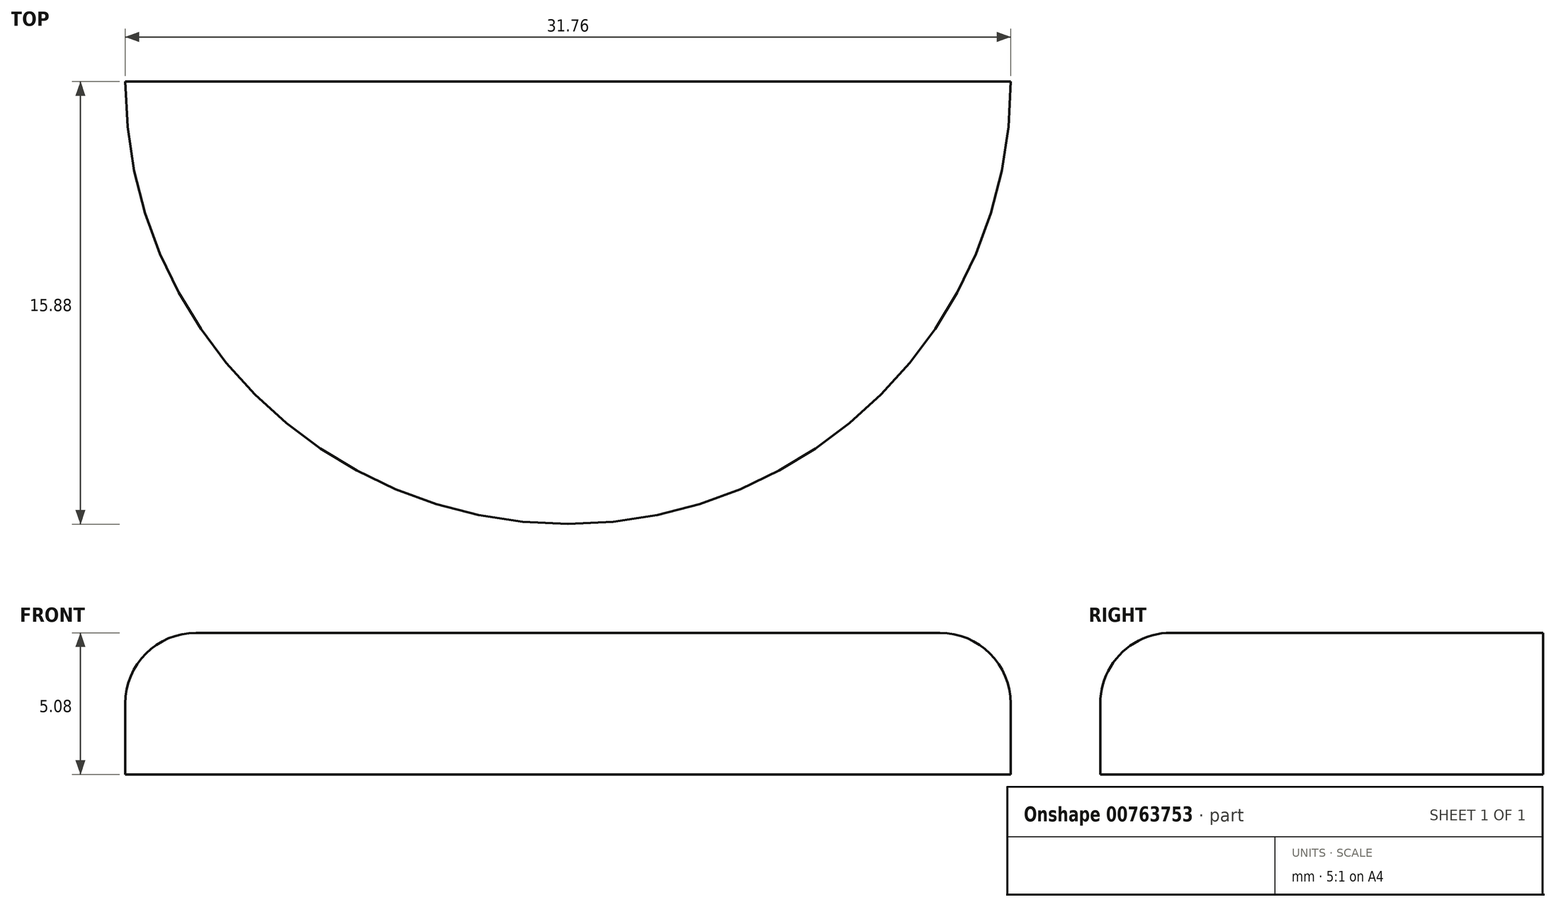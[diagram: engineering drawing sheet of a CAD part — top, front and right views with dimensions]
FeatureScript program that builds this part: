
annotation { "Feature Type Name" : "Feature", "Feature Type Description" : "" }
export const myFeature = defineFeature(function(context is Context, id is Id, definition is map)
    precondition{}
    {
        {
            var Q0;
            Q0=qCreatedBy(makeId("Top.planeOp"),FACE);
            var sketch = newSketch(context, id + "F0", { "sketchPlane" : qUnion([Q0])});
            skCircle(sketch, "E0", {"center": v(0, 0) * mm, "radius": 15.88 * mm});
            skLineSegment(sketch, "E1", {"start": v(15.88, 0) * mm, "end": v(-15.88, 0) * mm});
            skSolve(sketch);
        }
        {
            var Q0;
            {var subQ0=sQuery(id+"F0.wireOp",EDGE,"E1");Q0=makeQuery(id+"F0.imprint","IMPRINT",FACE,{"disambiguationData":[TD([[makeQuery(id+"F0.imprint","IMPRINT",EDGE,{"derivedFrom":subQ0}),1.0]])]});}
            extrude(context, id + "F1", {"entities" : qUnion([Q0]), "endBound" : BoundingType.SYMMETRIC, "depth" : 5.08 * mm, "offsetDistance" : 25.4 * mm});
        }
        {
            var Q0;
            Q0=makeQuery(id+"F1.opExtrude","SWEPT_FACE",FACE,{"disambiguationData":[OSD([sQuery(id+"F0.wireOp",EDGE,"E1")])]});
            var sketch = newSketch(context, id + "F2", { "sketchPlane" : qUnion([Q0])});
            skSolve(sketch);
        }
        {
            var Q0;
            {var subQ0=sQuery(id+"F0.wireOp",EDGE,"E1");Q0=makeQuery(id+"F2.imprint","IMPRINT",FACE,{"disambiguationData":[TD([[makeQuery(id+"F2.imprint","IMPRINT",EDGE,{"derivedFrom":makeQuery(id+"F1.opExtrude","CAP_EDGE",EDGE,{"disambiguationData":[OSD([subQ0])],"isStart":true})}),1.0]])]});}
            var sketch = newSketch(context, id + "F3", { "sketchPlane" : qUnion([Q0])});
            skCircle(sketch, "E2", {"center": v(7.9, 0) * mm, "radius": 2.54 * mm});
            skCircle(sketch, "E3", {"center": v(-13.33, 0) * mm, "radius": 2.54 * mm});
            skPoint(sketch, "E4", {"position": v(-15.88, 0) * mm});
            skLineSegment(sketch, "E5", {"start": v(0, 6.36) * mm, "end": v(0, -8.69) * mm});
            skPoint(sketch, "E6", {"position": v(13.37, 0) * mm});
            skCircle(sketch, "E7", {"center": v(13.37, 0) * mm, "radius": 2.54 * mm});
            skSolve(sketch);
        }
        {
            var Q0;
            Q0=sQuery(id+"F3.wireOp",EDGE,"E2");
            extrude(context, id + "F4", {"bodyType" : ToolBodyType.SURFACE, "surfaceEntities" : qUnion([Q0]), "endBound" : BoundingType.UP_TO_NEXT, "oppositeDirection" : true, "depth" : 25.4 * mm, "offsetDistance" : 25.4 * mm});
        }
        {
            var Q0;
            Q0=makeQuery(id+"F1.opExtrude","CAP_EDGE",EDGE,{"disambiguationData":[OSD([sQuery(id+"F0.wireOp",EDGE,"E0")])],"isStart":false});
            fillet(context, id + "F5", {"entities" : qUnion([Q0]), "radius" : 2.54 * mm, "tangentPropagation" : true, "allowEdgeOverflow" : false});
        }
        {
            var Q0;
            Q0=sQuery(id+"F3.wireOp",EDGE,"E3");
            var Q1;
            Q1=sQuery(id+"F3.wireOp",EDGE,"E5");
            revolve(context, id + "F6", {"bodyType" : ToolBodyType.SURFACE, "surfaceOperationType" : NewSurfaceOperationType.NEW, "surfaceEntities" : qUnion([Q0]), "axis" : qUnion([Q1]), "revolveType" : RevolveType.ONE_DIRECTION, "angle" : 180 * degree});
        }
    });
